AUTODESK INVENTOR PART (.ipt)
format: ipt  version: 2022.3 (Build 263350000, 350)  size: 267,776 bytes
history: native  units: mm
features: sketch x8, extrude x4, fillet x3, sweep x2, hole x1
ambient origin geometry x8: Origin, YZ Plane, XZ Plane, XY Plane, X Axis, Y Axis, Z Axis, Center Point
bodies: Solid1 (feature_tree)
feature tree (18):
  extrude  "Extrusion1"  Depth=74.0mm
  fillet  "Fillet1"  Radius=50.0mm
  fillet  "Fillet2"  Radius=10.0mm
  fillet  "Fillet3"  Radius=40.0mm
  extrude  "Extrusion2"  Depth=50.0mm TaperAngle=0.0deg
  hole  "Hole1"  [1 undecoded]
  sweep  "Sweep1"
  sweep  "Sweep2"
  sketch  "Sketch8"  dims[d18=5.0mm d19=3.4mm d20=3.4mm d21=3.4mm d22=3.4mm d23=50.0mm d24=0.0mm d25=3.4mm d26=6.0mm d27=6.0mm d28=2.0mm d29=90.0deg d30=2.2mm d31=0.0mm d32=8.0mm d33=8.0mm d34=20.0mm d35=5.0mm d36=20.0mm d37=9.0mm d38=0.0mm d39=0.0mm d40=0.0mm d41=0.0mm d42=8.0mm d43=8.0mm d44=20.0mm d45=5.0mm d46=20.0mm d47=9.0mm d48=0.0mm d49=0.0mm d50=10.0mm d51=20.0mm d52=8.0mm d53=8.0mm d54=5.0mm d55=0.0mm d56=0.0mm d57=0.0mm]
  extrude  "Extrusion3"  Depth=40.0mm
  extrude  "Extrusion4"  Depth=40.0mm
  sketch  "Sketch1"  dims[d0=20.0mm d1=74.0mm d2=50.0mm d3=10.0mm d4=40.0mm]
  sketch  "Sketch2"  dims[d5=10.0mm d6=50.0mm d7=0.0mm]
  sketch  "Sketch3"  dims[d8=10.0mm d9=5.0mm]
  sketch  "Sketch4"  dims[d10=10.0mm d11=10.0mm]
  sketch  "Sketch5"  dims[d12=5.0mm d13=10.0mm]
  sketch  "Sketch6"  dims[d14=5.0mm d15=40.0mm]
  sketch  "Sketch7"  dims[d16=5.0mm d17=40.0mm]
note: 1 required parameter value undecoded (feature->parameter linkage not recoverable at this tier; creation-order binding heuristic only, values carry confidence <= 0.55)
